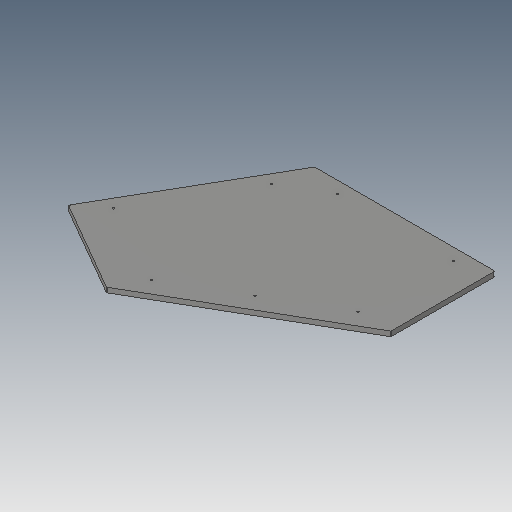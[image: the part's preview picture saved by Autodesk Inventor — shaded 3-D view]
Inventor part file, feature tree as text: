
AUTODESK INVENTOR PART (.ipt)
format: ipt  version: 2023.5 (Build 275446000, 446)  size: 94,208 bytes
history: native  units: in
note: dims shown in document units (in); Inventor stores cm internally (conversion verified against a paired STEP export)
features: fillet x1
ambient origin geometry x8: Origin, YZ Plane, XZ Plane, XY Plane, X Axis, Y Axis, Z Axis, Center Point
bodies: Solid1 (feature_tree)
feature tree (1):
  fillet  "Fillet1"  [1 undecoded]
note: 1 required parameter value undecoded (feature->parameter linkage not recoverable at this tier; creation-order binding heuristic only, values carry confidence <= 0.55)
